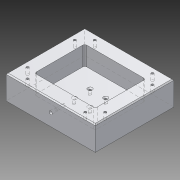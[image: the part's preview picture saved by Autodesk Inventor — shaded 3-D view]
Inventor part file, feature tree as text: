
AUTODESK INVENTOR PART (.ipt)
format: ipt  version: 2013 (Build 170138000, 138)  size: 188,928 bytes
history: native  units: mm
features: sketch x5, extrude x3, hole x2, fillet x1, chamfer x1
ambient origin geometry x8: Origin, YZ Plane, XZ Plane, XY Plane, X Axis, Y Axis, Z Axis, Center Point
bodies: Volumenkörper1 (feature_tree)
feature tree (12):
  extrude  "Extrusion1"  Depth=150.0mm
  extrude  "Extrusion2"  Depth=116.0mm
  fillet  "Rundung1"  Radius=96.0mm
  chamfer  "Fase1"  Distance=36.0mm
  extrude  "Extrusion4"  Depth=2.0mm TaperAngle=45.0deg
  hole  "Bohrung1"  [1 undecoded]
  hole  "Bohrung2"  [1 undecoded]
  sketch  "Skizze1"  dims[d0=170.0mm d2=150.0mm]
  sketch  "Skizze2"  dims[d3=46.0mm d4=0.0mm d5=116.0mm d7=96.0mm d8=36.0mm d9=0.0mm]
  sketch  "Skizze4"  dims[d10=4.0mm d11=2.0mm d12=2.0mm d13=45.0deg]
  sketch  "Skizze5"  dims[d14=8.0mm d15=30.0mm]
  sketch  "Skizze7"  dims[d16=30.0mm d17=8.0mm d18=8.0mm d19=30.0mm d20=8.0mm d21=30.0mm d22=30.0mm d23=8.0mm d24=8.0mm d25=30.0mm d26=8.0mm d27=30.0mm d28=30.0mm d29=8.0mm d30=4.0mm d31=4.0mm d32=4.0mm d33=4.0mm d34=4.0mm d35=4.0mm d36=4.0mm d37=4.0mm d56=4.5mm d57=4.5mm d58=4.5mm d59=4.5mm d60=4.5mm d61=4.5mm d62=4.5mm d63=4.5mm d66=12.0mm d67=0.0mm d68=15.0mm d69=15.0mm d70=30.0mm d71=30.0mm d72=30.0mm d73=30.0mm d74=15.0mm d75=15.0mm d76=4.5mm d77=6.0mm d78=8.6mm d79=2.0mm d80=90.0deg d81=15.0mm d82=20.594885mm d83=23.0mm d84=85.0mm d85=4.0mm d86=6.0mm d87=6.0mm d88=10.0mm d89=90.0deg d90=30.0mm d91=20.594885mm d92=30.0mm d93=30.0mm d94=11.0mm d95=11.0mm d96=11.0mm d97=11.0mm d98=148.0mm d99=30.0mm d100=30.0mm d101=11.0mm d102=11.0mm d103=11.0mm d104=11.0mm d105=128.0mm d106=128.0mm d107=30.0mm d108=30.0mm d109=30.0mm d110=30.0mm]
note: 2 required parameter values undecoded (feature->parameter linkage not recoverable at this tier; creation-order binding heuristic only, values carry confidence <= 0.55)
